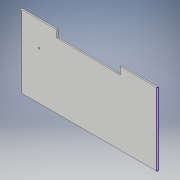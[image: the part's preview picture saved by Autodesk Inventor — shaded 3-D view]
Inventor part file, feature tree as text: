
AUTODESK INVENTOR PART (.ipt)
format: ipt  version: 2019 (Build 230136000, 136)  size: 109,056 bytes
history: native  units: in
note: dims shown in document units (in); Inventor stores cm internally (conversion verified against a paired STEP export)
features: sketch x5, extrude x3
ambient origin geometry x8: Origin, YZ Plane, XZ Plane, XY Plane, X Axis, Y Axis, Z Axis, Center Point
bodies: Solid1 (feature_tree)
feature tree (8):
  extrude  "Extrusion1"  Depth=0.1969in TaperAngle=0.0deg
  extrude  "Extrusion2"  [1 undecoded]
  extrude  "Extrusion3"  [1 undecoded]
  sketch  "Sketch4"
  sketch  "Sketch5"
  sketch  "Sketch1"  dims[d6=0.1969in d7=0.0in d11=0.1969in d12=0.0in]
  sketch  "Sketch2"  dims[d13=0.1969in d14=0.0in]
  sketch  "Sketch3"
note: 2 required parameter values undecoded (feature->parameter linkage not recoverable at this tier; creation-order binding heuristic only, values carry confidence <= 0.55)
